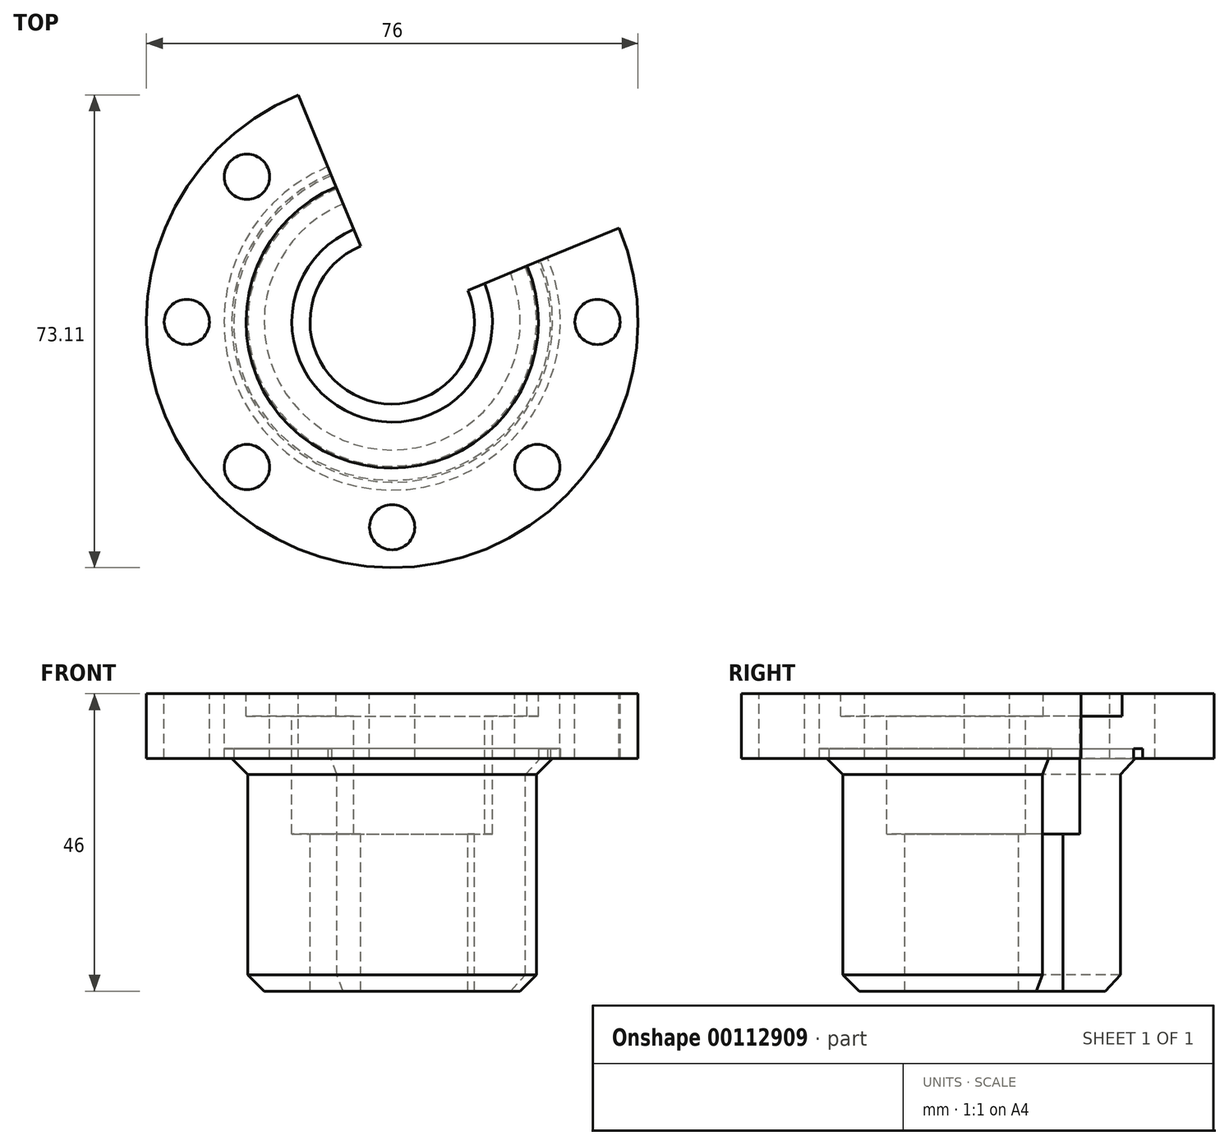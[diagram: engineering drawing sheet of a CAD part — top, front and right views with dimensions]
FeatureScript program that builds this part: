
annotation { "Feature Type Name" : "Feature", "Feature Type Description" : "" }
export const myFeature = defineFeature(function(context is Context, id is Id, definition is map)
    precondition{}
    {
        {
            var Q0;
            Q0=qCreatedBy(makeId("Front.planeOp"),FACE);
            var sketch = newSketch(context, id + "F0", { "sketchPlane" : qUnion([Q0])});
            skLineSegment(sketch, "E0", {"start": v(0, 27.4) * mm, "end": v(0, -63.72) * mm});
            skLineSegment(sketch, "E1", {"start": v(22.6, 42.84) * mm, "end": v(38, 42.84) * mm});
            skLineSegment(sketch, "E2", {"start": v(38, 42.84) * mm, "end": v(38, 32.84) * mm});
            skLineSegment(sketch, "E3", {"start": v(22.6, 42.84) * mm, "end": v(22.6, 39.34) * mm});
            skLineSegment(sketch, "E4", {"start": v(22.6, 39.34) * mm, "end": v(15.5, 39.34) * mm});
            skLineSegment(sketch, "E5", {"start": v(15.5, 39.34) * mm, "end": v(15.5, 13.34) * mm});
            skLineSegment(sketch, "E6", {"start": v(12.7, 13.34) * mm, "end": v(12.7, -3.16) * mm});
            skLineSegment(sketch, "E7", {"start": v(22.3, -3.16) * mm, "end": v(22.3, 32.84) * mm});
            skLineSegment(sketch, "E8", {"start": v(22.3, 32.84) * mm, "end": v(38, 32.84) * mm});
            skLineSegment(sketch, "E9", {"start": v(12.7, 13.34) * mm, "end": v(15.5, 13.34) * mm});
            skLineSegment(sketch, "E10", {"start": v(12.7, -3.16) * mm, "end": v(22.3, -3.16) * mm});
            skLineSegment(sketch, "E11", {"start": v(18.4, -3.16) * mm, "end": v(22.3, -3.16) * mm});
            skSolve(sketch);
        }
        {
            var Q0;
            Q0=makeQuery(id+"F0.imprint","IMPRINT",FACE,{"disambiguationData":[TD([[makeQuery(id+"F0.imprint","IMPRINT",EDGE,{"derivedFrom":sQuery(id+"F0.wireOp",EDGE,"E1")}),-1.0]])]});
            var Q1;
            Q1=sQuery(id+"F0.wireOp",EDGE,"E0");
            revolve(context, id + "F1", {"entities" : qUnion([Q0]), "axis" : qUnion([Q1]), "revolveType" : RevolveType.FULL});
        }
        {
            var Q0;
            Q0=makeQuery(id+"F1.opRevolve","SWEPT_FACE",FACE,{"disambiguationData":[OSD([sQuery(id+"F0.wireOp",EDGE,"E1")])]});
            var sketch = newSketch(context, id + "F2", { "sketchPlane" : qUnion([Q0])});
            skPoint(sketch, "E12.middle", {"position": v(0, 0) * mm});
            skCircle(sketch, "E13", {"center": v(0, 31.75) * mm, "radius": 3.5 * mm});
            skCircle(sketch, "E14", {"center": v(0, -31.75) * mm, "radius": 3.5 * mm});
            skCircle(sketch, "E15", {"center": v(31.75, 0) * mm, "radius": 3.5 * mm});
            skCircle(sketch, "E16", {"center": v(-31.75, 0) * mm, "radius": 3.5 * mm});
            skCircle(sketch, "E17", {"center": v(-22.45, 22.45) * mm, "radius": 3.5 * mm});
            skCircle(sketch, "E18", {"center": v(22.45, 22.45) * mm, "radius": 3.5 * mm});
            skCircle(sketch, "E19", {"center": v(22.45, -22.45) * mm, "radius": 3.5 * mm});
            skCircle(sketch, "E20", {"center": v(-22.45, -22.45) * mm, "radius": 3.5 * mm});
            skSolve(sketch);
        }
        {
            var Q0;
            Q0 = qSketchRegion(id + "F2", true);
            extrude(context, id + "F3", {"entities" : qUnion([Q0]), "operationType" : NewBodyOperationType.REMOVE, "oppositeDirection" : true, "depth" : 25 * mm});
        }
        {
            var Q0;
            Q0=makeQuery(id+"F1.opRevolve","SWEPT_EDGE",EDGE,{"disambiguationData":[OSD([sQuery(id+"F0.wireOp",EDGE,"E7"),sQuery(id+"F0.wireOp",EDGE,"E11")])]});
            chamfer(context, id + "F4", {"entities" : qUnion([Q0]), "width" : 2.5 * mm, "tangentPropagation" : true});
        }
        {
            var Q0;
            Q0=makeQuery(id+"F1.opRevolve","SWEPT_FACE",FACE,{"disambiguationData":[OSD([sQuery(id+"F0.wireOp",EDGE,"E8")])]});
            var sketch = newSketch(context, id + "F5", { "sketchPlane" : qUnion([Q0])});
            skCircle(sketch, "E21", {"center": v(0, 0) * mm, "radius": 26 * mm});
            skCircle(sketch, "E22", {"center": v(0, 0) * mm, "radius": 24.5 * mm});
            skSolve(sketch);
        }
        {
            var Q0;
            Q0 = qSketchRegion(id + "F5", true);
            extrude(context, id + "F6", {"entities" : qUnion([Q0]), "operationType" : NewBodyOperationType.REMOVE, "oppositeDirection" : true, "depth" : 1.5 * mm});
        }
        {
            var Q0;
            Q0=makeQuery(id+"F1.opRevolve","SWEPT_FACE",FACE,{"disambiguationData":[OSD([sQuery(id+"F0.wireOp",EDGE,"E1")])]});
            var sketch = newSketch(context, id + "F7", { "sketchPlane" : qUnion([Q0])});
            skLineSegment(sketch, "E23", {"start": v(-11.23, 27.1) * mm, "end": v(0, 0) * mm});
            skLineSegment(sketch, "E24", {"start": v(27.1, 11.23) * mm, "end": v(0, 0) * mm});
            skLineSegment(sketch, "E25", {"start": v(27.1, 11.23) * mm, "end": v(39.63, 16.42) * mm});
            skLineSegment(sketch, "E26", {"start": v(39.63, 16.42) * mm, "end": v(25.74, 40.47) * mm});
            skLineSegment(sketch, "E27", {"start": v(21.04, 40.47) * mm, "end": v(25.74, 40.47) * mm});
            skLineSegment(sketch, "E28", {"start": v(0, 0) * mm, "end": v(39.63, 16.42) * mm});
            skLineSegment(sketch, "E29", {"start": v(0, 0) * mm, "end": v(-17.76, 42.87) * mm});
            skLineSegment(sketch, "E30", {"start": v(-17.76, 42.87) * mm, "end": v(25.74, 40.47) * mm});
            skSolve(sketch);
        }
        {
            var Q0;
            Q0 = qSketchRegion(id + "F7", true);
            extrude(context, id + "F8", {"entities" : qUnion([Q0]), "operationType" : NewBodyOperationType.REMOVE, "endBound" : BoundingType.THROUGH_ALL, "oppositeDirection" : true, "depth" : 25 * mm});
        }
        {
            var Q0;
            Q0=makeQuery(id+"F1.opRevolve","SWEPT_FACE",FACE,{"disambiguationData":[OSD([sQuery(id+"F0.wireOp",EDGE,"E9")])]});
            extrude(context, id + "F9", {"entities" : qUnion([Q0]), "operationType" : NewBodyOperationType.ADD, "depth" : 7.8 * mm});
        }
    });
